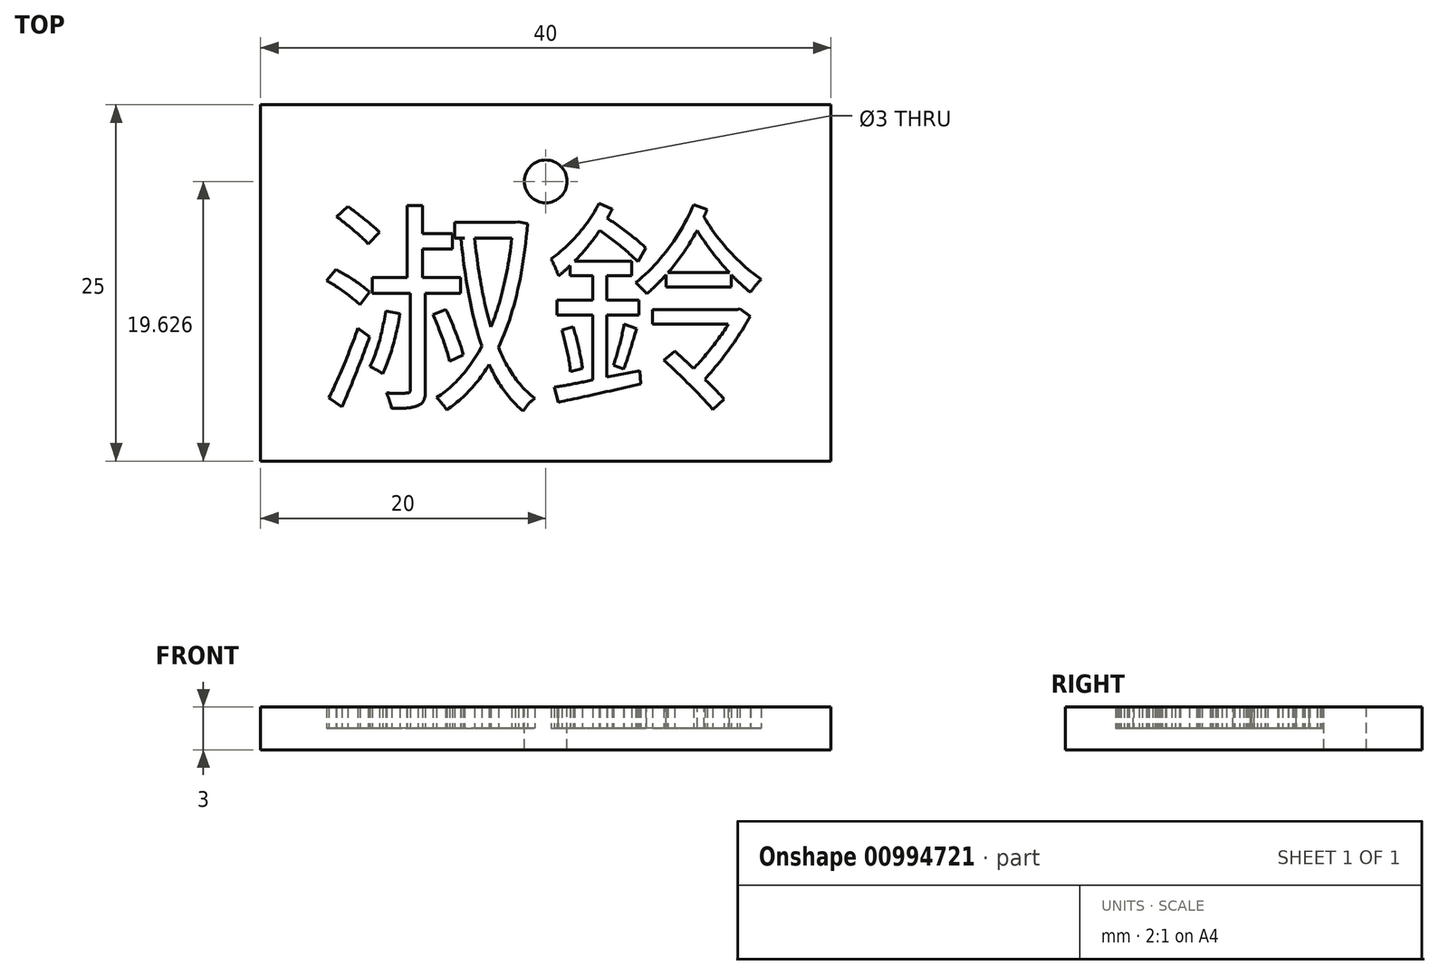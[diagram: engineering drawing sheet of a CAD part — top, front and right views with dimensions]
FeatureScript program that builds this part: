
annotation { "Feature Type Name" : "Feature", "Feature Type Description" : "" }
export const myFeature = defineFeature(function(context is Context, id is Id, definition is map)
    precondition{}
    {
        {
            var Q0;
            Q0=qCreatedBy(makeId("Top.planeOp"),FACE);
            var sketch = newSketch(context, id + "F0", { "sketchPlane" : qUnion([Q0])});
            skLineSegment(sketch, "E0.bottom", {"start": v(-20, -12.5) * mm, "end": v(20, -12.5) * mm});
            skLineSegment(sketch, "E0.top", {"start": v(-20, 12.5) * mm, "end": v(20, 12.5) * mm});
            skLineSegment(sketch, "E0.left", {"start": v(-20, -12.5) * mm, "end": v(-20, 12.5) * mm});
            skLineSegment(sketch, "E0.right", {"start": v(20, -12.5) * mm, "end": v(20, 12.5) * mm});
            skPoint(sketch, "E0.middle", {"position": v(0, 0) * mm});
            skSolve(sketch);
        }
        {
            var Q0;
            Q0 = qSketchRegion(id + "F0", true);
            extrude(context, id + "F1", {"entities" : qUnion([Q0]), "depth" : 3 * mm, "offsetDistance" : 25 * mm});
        }
        {
            var Q0;
            Q0=makeQuery(id+"F1.opExtrude","CAP_FACE",FACE,{"disambiguationData":[OSD([sQuery(id+"F0.wireOp",EDGE,"E0.bottom"),sQuery(id+"F0.wireOp",EDGE,"E0.top"),sQuery(id+"F0.wireOp",EDGE,"E0.left"),sQuery(id+"F0.wireOp",EDGE,"E0.right")])],"isStart":false});
            var sketch = newSketch(context, id + "F2", { "sketchPlane" : qUnion([Q0])});
            skLineSegment(sketch, "E1.0", {"start": v(18, -12.5) * mm, "end": v(18, 12.5) * mm});
            skLineSegment(sketch, "E2.0", {"start": v(-25, -12.5) * mm, "end": v(-25, 12.5) * mm});
            skLineSegment(sketch, "E3.0", {"start": v(18, 10.5) * mm, "end": v(-18, 10.5) * mm});
            skLineSegment(sketch, "E3.1", {"start": v(18, -10.5) * mm, "end": v(18, 10.5) * mm});
            skLineSegment(sketch, "E3.2", {"start": v(-18, -10.5) * mm, "end": v(18, -10.5) * mm});
            skLineSegment(sketch, "E3.3", {"start": v(-18, 10.5) * mm, "end": v(-18, -10.5) * mm});
            skSolve(sketch);
        }
        {
            var Q0;
            Q0 = qSketchRegion(id + "F2", true);
            extrude(context, id + "F3", {"entities" : qUnion([Q0]), "operationType" : NewBodyOperationType.REMOVE, "oppositeDirection" : true, "depth" : 1.5 * mm, "offsetDistance" : 25 * mm});
        }
        {
            var Q0;
            Q0=makeQuery(id+"F3.boolean.opBoolean","COPY",FACE,{"derivedFrom":makeQuery(id+"F3.opExtrude","CAP_FACE",FACE,{"disambiguationData":[OSD([sQuery(id+"F2.wireOp",EDGE,"E3.0"),sQuery(id+"F2.wireOp",EDGE,"E3.2"),sQuery(id+"F2.wireOp",EDGE,"E3.3"),sQuery(id+"F2.wireOp",EDGE,"E1.0")])],"isStart":false})});
            var sketch = newSketch(context, id + "F4", { "sketchPlane" : qUnion([Q0])});
            skCircle(sketch, "E4", {"center": v(0, 7.13) * mm, "radius": 1.5 * mm});
            skSolve(sketch);
        }
        {
            var Q0;
            Q0=makeQuery(id+"F4.imprint","IMPRINT",FACE,{"disambiguationData":[TD([[makeQuery(id+"F4.imprint","IMPRINT",EDGE,{"derivedFrom":sQuery(id+"F4.wireOp",EDGE,"E4")}),1.0]])]});
            extrude(context, id + "F5", {"entities" : qUnion([Q0]), "operationType" : NewBodyOperationType.ADD, "depth" : 1.5 * mm, "offsetDistance" : 25 * mm});
        }
        {
            var Q0;
            Q0=makeQuery(id+"F5.opExtrude","CAP_FACE",FACE,{"disambiguationData":[OSD([sQuery(id+"F4.wireOp",EDGE,"E4")])],"isStart":false});
            extrude(context, id + "F6", {"entities" : qUnion([Q0]), "operationType" : NewBodyOperationType.REMOVE, "endBound" : BoundingType.THROUGH_ALL, "oppositeDirection" : true, "depth" : 25 * mm, "offsetDistance" : 25 * mm});
        }
        {
            var Q0;
            Q0=makeQuery(id+"F3.boolean.opBoolean","COPY",FACE,{"derivedFrom":makeQuery(id+"F3.opExtrude","CAP_FACE",FACE,{"disambiguationData":[OSD([sQuery(id+"F2.wireOp",EDGE,"E3.0"),sQuery(id+"F2.wireOp",EDGE,"E3.2"),sQuery(id+"F2.wireOp",EDGE,"E3.3"),sQuery(id+"F2.wireOp",EDGE,"E1.0")])],"isStart":false})});
            var sketch = newSketch(context, id + "F7", { "sketchPlane" : qUnion([Q0])});
            skText(sketch, "E5", { "text": "淑鈴", "fontName": "NotoSansCJKtc-Regular.otf"});
            const initialGuessF7  = {"E5": [-0.01598, -0.00771, 1, 0, 0.01138]};
            skSetInitialGuess(sketch, initialGuessF7);
            skSolve(sketch);
        }
        {
            var Q0;
            Q0=makeQuery(id+"F7.imprint","IMPRINT",FACE,{"disambiguationData":[TD([[makeQuery(id+"F7.imprint","IMPRINT",EDGE,{"derivedFrom":sQuery(id+"F7.wireOp",EDGE,"E5.sketch_text.stroke-0")}),-1.0]])]});
            var Q1;
            Q1=makeQuery(id+"F7.imprint","IMPRINT",FACE,{"disambiguationData":[TD([[makeQuery(id+"F7.imprint","IMPRINT",EDGE,{"derivedFrom":sQuery(id+"F7.wireOp",EDGE,"E5.sketch_text.stroke-40")}),-1.0]])]});
            var Q2;
            Q2=makeQuery(id+"F7.imprint","IMPRINT",FACE,{"disambiguationData":[TD([[makeQuery(id+"F7.imprint","IMPRINT",EDGE,{"derivedFrom":sQuery(id+"F7.wireOp",EDGE,"E5.sketch_text.stroke-106")}),-1.0]])]});
            extrude(context, id + "F8", {"entities" : qUnion([Q0, Q1, Q2]), "operationType" : NewBodyOperationType.ADD, "depth" : 1.5 * mm, "offsetDistance" : 25 * mm});
        }
    });
